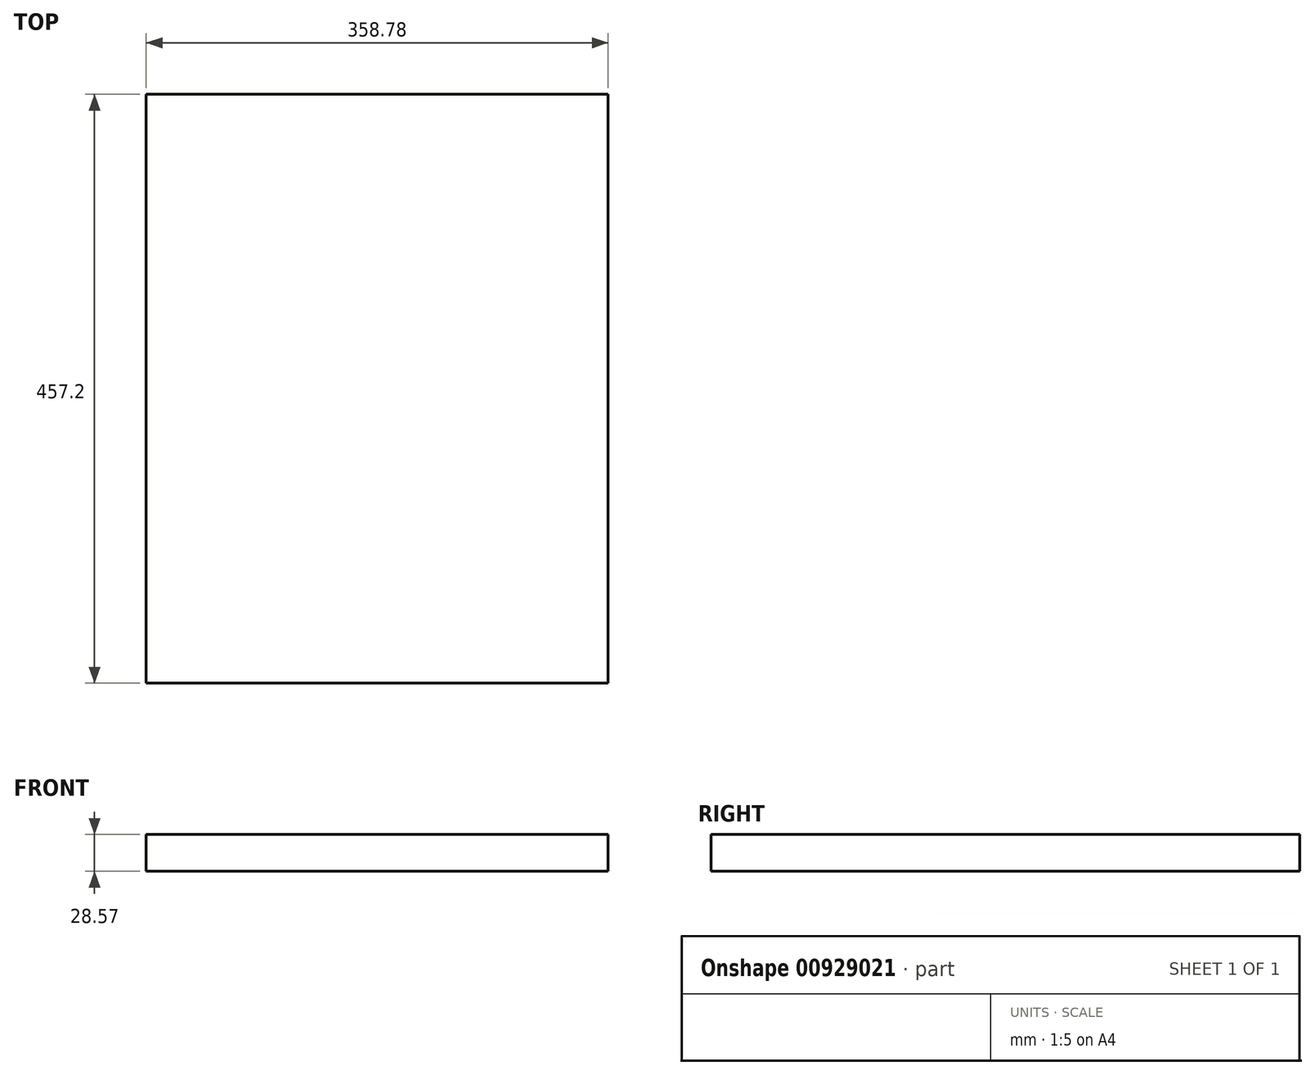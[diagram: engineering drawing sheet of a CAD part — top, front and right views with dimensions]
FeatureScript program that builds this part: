
annotation { "Feature Type Name" : "Feature", "Feature Type Description" : "" }
export const myFeature = defineFeature(function(context is Context, id is Id, definition is map)
    precondition{}
    {
        {
            var Q0;
            Q0=qCreatedBy(makeId("Top.planeOp"),FACE);
            var sketch = newSketch(context, id + "F0", { "sketchPlane" : qUnion([Q0])});
            skLineSegment(sketch, "E0.bottom", {"start": v(179.39, 228.6) * mm, "end": v(-179.39, 228.6) * mm});
            skLineSegment(sketch, "E0.top", {"start": v(179.39, -228.6) * mm, "end": v(-179.39, -228.6) * mm});
            skLineSegment(sketch, "E0.left", {"start": v(179.39, 228.6) * mm, "end": v(179.39, -228.6) * mm});
            skLineSegment(sketch, "E0.right", {"start": v(-179.39, 228.6) * mm, "end": v(-179.39, -228.6) * mm});
            skPoint(sketch, "E0.middle", {"position": v(0, 0) * mm});
            skSolve(sketch);
        }
        {
            var Q0;
            Q0=makeQuery(id+"F0.imprint","IMPRINT",FACE,{"disambiguationData":[TD([[makeQuery(id+"F0.imprint","IMPRINT",EDGE,{"derivedFrom":sQuery(id+"F0.wireOp",EDGE,"E0.bottom")}),1.0]])]});
            extrude(context, id + "F1", {"entities" : qUnion([Q0]), "depth" : 28.57 * mm, "offsetDistance" : 25.4 * mm});
        }
    });
